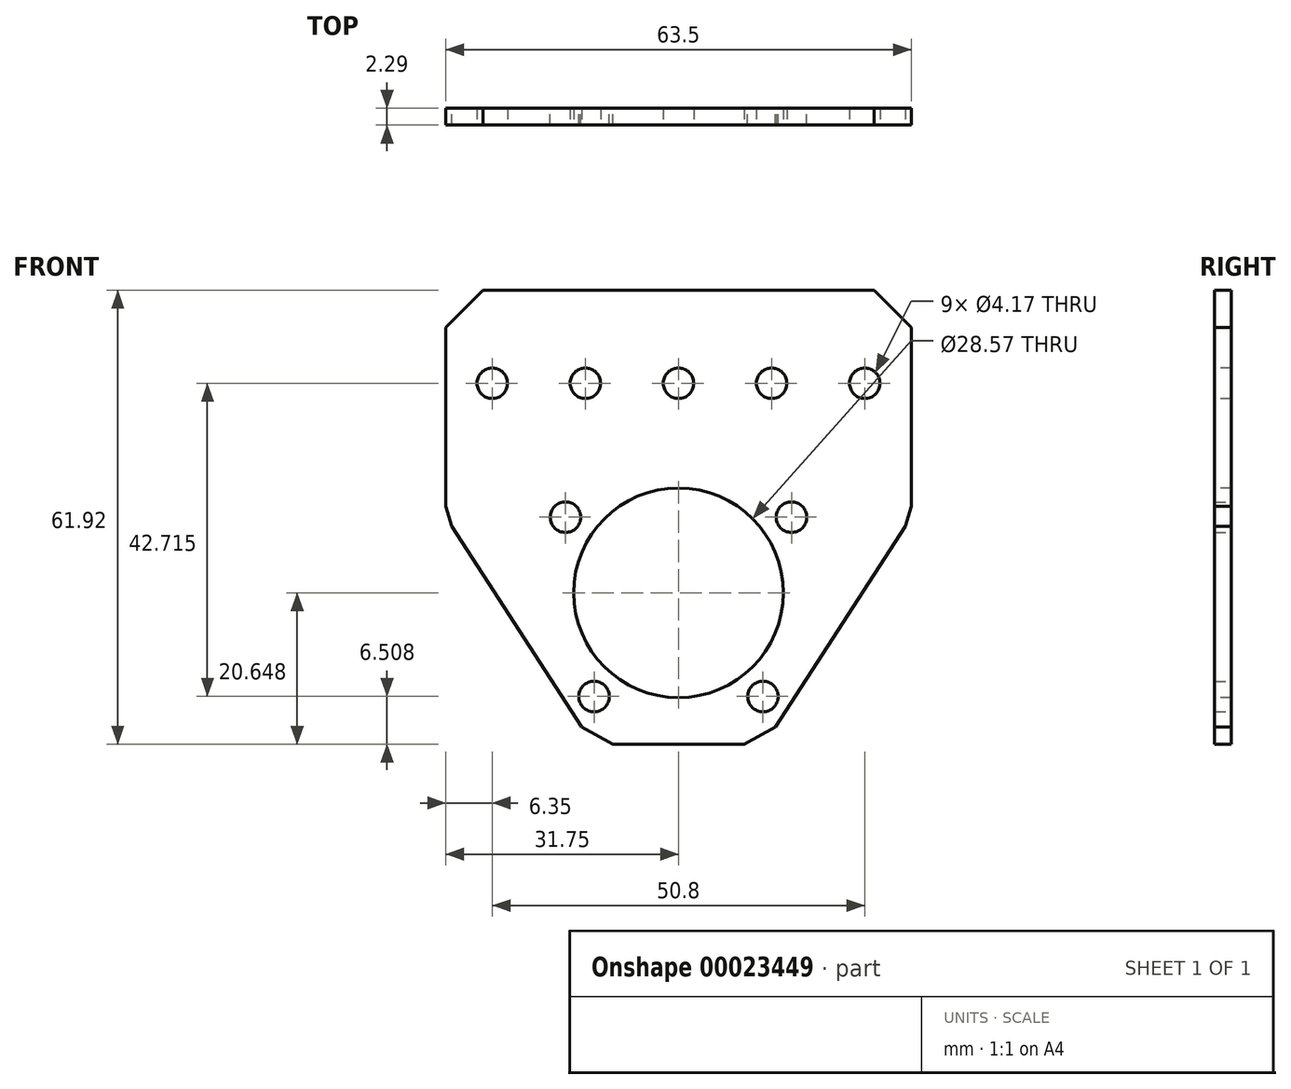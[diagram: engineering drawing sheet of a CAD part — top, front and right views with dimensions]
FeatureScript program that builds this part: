
annotation { "Feature Type Name" : "Feature", "Feature Type Description" : "" }
export const myFeature = defineFeature(function(context is Context, id is Id, definition is map)
    precondition{}
    {
        {
            var Q0;
            Q0=qCreatedBy(makeId("Front.planeOp"),FACE);
            var sketch = newSketch(context, id + "F0", { "sketchPlane" : qUnion([Q0])});
            skLineSegment(sketch, "E0", {"start": v(-31.75, 30.96) * mm, "end": v(31.75, 30.96) * mm});
            skLineSegment(sketch, "E1", {"start": v(31.75, 30.96) * mm, "end": v(31.75, 0) * mm});
            skLineSegment(sketch, "E2", {"start": v(31.75, 0) * mm, "end": v(11.7, -30.96) * mm});
            skLineSegment(sketch, "E3", {"start": v(11.7, -30.96) * mm, "end": v(-11.7, -30.96) * mm});
            skLineSegment(sketch, "E4", {"start": v(-11.7, -30.96) * mm, "end": v(-31.75, 0) * mm});
            skLineSegment(sketch, "E5", {"start": v(-31.75, 0) * mm, "end": v(-31.75, 30.96) * mm});
            skLineSegment(sketch, "E6", {"start": v(0, 34.06) * mm, "end": v(0, -68.88) * mm, "construction": true});
            skLineSegment(sketch, "E7", {"start": v(-50.48, 0) * mm, "end": v(68.05, 0) * mm, "construction": true});
            skSolve(sketch);
        }
        {
            var Q0;
            Q0=makeQuery(id+"F0.imprint","IMPRINT",FACE,{"disambiguationData":[TD([[makeQuery(id+"F0.imprint","IMPRINT",EDGE,{"derivedFrom":sQuery(id+"F0.wireOp",EDGE,"E0")}),-1.0]])]});
            extrude(context, id + "F1", {"entities" : qUnion([Q0]), "depth" : 2.3 * mm});
        }
        {
            var Q0;
            Q0=makeQuery(id+"F1.opExtrude","CAP_FACE",FACE,{"disambiguationData":[OSD([sQuery(id+"F0.wireOp",EDGE,"E0"),sQuery(id+"F0.wireOp",EDGE,"E1"),sQuery(id+"F0.wireOp",EDGE,"E2"),sQuery(id+"F0.wireOp",EDGE,"E3"),sQuery(id+"F0.wireOp",EDGE,"E4"),sQuery(id+"F0.wireOp",EDGE,"E5")])],"isStart":false});
            var sketch = newSketch(context, id + "F2", { "sketchPlane" : qUnion([Q0])});
            skCircle(sketch, "E8", {"center": v(0, -10.31) * mm, "radius": 14.29 * mm});
            skLineSegment(sketch, "E9", {"start": v(-40.4, 18.26) * mm, "end": v(50.03, 18.26) * mm, "construction": true});
            skCircle(sketch, "E10", {"center": v(0, -10.31) * mm, "radius": 18.41 * mm});
            skSolve(sketch);
        }
        {
            var Q0;
            Q0=sQuery(id+"F2.wireOp",VERTEX,"E8.center");
            var Q1;
            Q1=makeQuery(id+"F1.opExtrude","SWEPT_BODY",BODY,{"disambiguationData":[OSD([sQuery(id+"F0.wireOp",EDGE,"E0"),sQuery(id+"F0.wireOp",EDGE,"E1"),sQuery(id+"F0.wireOp",EDGE,"E2"),sQuery(id+"F0.wireOp",EDGE,"E3"),sQuery(id+"F0.wireOp",EDGE,"E4"),sQuery(id+"F0.wireOp",EDGE,"E5")])]});
            hole(context, id + "F3", {"style" : HoleStyle.SIMPLE, "holeDiameter" : 28.57 * mm, "endStyle" : HoleEndStyle.THROUGH, "locations" : qUnion([Q0]), "scope" : qUnion([Q1])});
        }
        {
            var Q0;
            Q0=makeQuery(id+"F1.opExtrude","CAP_FACE",FACE,{"disambiguationData":[OSD([sQuery(id+"F0.wireOp",EDGE,"E0"),sQuery(id+"F0.wireOp",EDGE,"E1"),sQuery(id+"F0.wireOp",EDGE,"E2"),sQuery(id+"F0.wireOp",EDGE,"E3"),sQuery(id+"F0.wireOp",EDGE,"E4"),sQuery(id+"F0.wireOp",EDGE,"E5")])],"isStart":false});
            var sketch = newSketch(context, id + "F4", { "sketchPlane" : qUnion([Q0])});
            skLineSegment(sketch, "E11", {"start": v(-84.78, 18.26) * mm, "end": v(95.41, 18.26) * mm});
            skPoint(sketch, "E12", {"position": v(25.4, 18.26) * mm});
            skPoint(sketch, "E13", {"position": v(12.7, 18.26) * mm});
            skPoint(sketch, "E14", {"position": v(0, 18.26) * mm});
            skPoint(sketch, "E15", {"position": v(-25.4, 18.26) * mm});
            skPoint(sketch, "E16", {"position": v(-12.7, 18.26) * mm});
            skPoint(sketch, "E17", {"position": v(-31.75, 18.26) * mm});
            skPoint(sketch, "E18", {"position": v(31.75, 18.26) * mm});
            skSolve(sketch);
        }
        {
            var Q0;
            Q0=sQuery(id+"F4.wireOp",VERTEX,"E15");
            var Q1;
            Q1=sQuery(id+"F4.wireOp",VERTEX,"E16");
            var Q2;
            Q2=sQuery(id+"F4.wireOp",VERTEX,"E14");
            var Q3;
            Q3=sQuery(id+"F4.wireOp",VERTEX,"E13");
            var Q4;
            Q4=sQuery(id+"F4.wireOp",VERTEX,"E12");
            var Q5;
            Q5=makeQuery(id+"F1.opExtrude","SWEPT_BODY",BODY,{"disambiguationData":[OSD([sQuery(id+"F0.wireOp",EDGE,"E0"),sQuery(id+"F0.wireOp",EDGE,"E1"),sQuery(id+"F0.wireOp",EDGE,"E2"),sQuery(id+"F0.wireOp",EDGE,"E3"),sQuery(id+"F0.wireOp",EDGE,"E4"),sQuery(id+"F0.wireOp",EDGE,"E5")])]});
            hole(context, id + "F5", {"style" : HoleStyle.SIMPLE, "holeDiameter" : 4.17 * mm, "endStyle" : HoleEndStyle.THROUGH, "locations" : qUnion([Q0, Q1, Q2, Q3, Q4]), "scope" : qUnion([Q5])});
        }
        {
            var Q0;
            Q0=qCreatedBy(makeId("Front.planeOp"),FACE);
            var sketch = newSketch(context, id + "F6", { "sketchPlane" : qUnion([Q0])});
            skCircle(sketch, "E19", {"center": v(0, -10.08) * mm, "radius": 18.41 * mm});
            skLineSegment(sketch, "E20", {"start": v(-37.76, 18.5) * mm, "end": v(42.16, 18.5) * mm});
            skPoint(sketch, "E21", {"position": v(31.72, 31.2) * mm});
            skPoint(sketch, "E22", {"position": v(-15.4, 0) * mm});
            skPoint(sketch, "E23", {"position": v(11.52, -24.45) * mm});
            skPoint(sketch, "E24", {"position": v(-11.52, -24.45) * mm});
            skLineSegment(sketch, "E25", {"start": v(0, -40.48) * mm, "end": v(0, 36.9) * mm});
            skLineSegment(sketch, "E26", {"start": v(48.02, -10.08) * mm, "end": v(-38.6, -10.08) * mm});
            skPoint(sketch, "E27", {"position": v(15.4, 0) * mm});
            skSolve(sketch);
        }
        {
            var Q0;
            Q0=sQuery(id+"F6.wireOp",VERTEX,"E22");
            var Q1;
            Q1=sQuery(id+"F6.wireOp",VERTEX,"E27");
            var Q2;
            Q2=sQuery(id+"F6.wireOp",VERTEX,"E23");
            var Q3;
            Q3=sQuery(id+"F6.wireOp",VERTEX,"E24");
            var Q4;
            Q4=makeQuery(id+"F1.opExtrude","SWEPT_BODY",BODY,{"disambiguationData":[OSD([sQuery(id+"F0.wireOp",EDGE,"E0"),sQuery(id+"F0.wireOp",EDGE,"E1"),sQuery(id+"F0.wireOp",EDGE,"E2"),sQuery(id+"F0.wireOp",EDGE,"E3"),sQuery(id+"F0.wireOp",EDGE,"E4"),sQuery(id+"F0.wireOp",EDGE,"E5")])]});
            hole(context, id + "F7", {"style" : HoleStyle.SIMPLE, "holeDiameter" : 4.17 * mm, "endStyle" : HoleEndStyle.THROUGH, "oppositeDirection" : true, "locations" : qUnion([Q0, Q1, Q2, Q3]), "scope" : qUnion([Q4])});
        }
        {
            var Q0;
            Q0=makeQuery(id+"F1.opExtrude","SWEPT_EDGE",EDGE,{"disambiguationData":[OSD([sQuery(id+"F0.wireOp",EDGE,"E0"),sQuery(id+"F0.wireOp",EDGE,"E5")])]});
            var Q1;
            Q1=makeQuery(id+"F1.opExtrude","SWEPT_EDGE",EDGE,{"disambiguationData":[OSD([sQuery(id+"F0.wireOp",EDGE,"E4"),sQuery(id+"F0.wireOp",EDGE,"E5")])]});
            var Q2;
            Q2=makeQuery(id+"F1.opExtrude","SWEPT_EDGE",EDGE,{"disambiguationData":[OSD([sQuery(id+"F0.wireOp",EDGE,"E3"),sQuery(id+"F0.wireOp",EDGE,"E4")])]});
            var Q3;
            Q3=makeQuery(id+"F1.opExtrude","SWEPT_EDGE",EDGE,{"disambiguationData":[OSD([sQuery(id+"F0.wireOp",EDGE,"E2"),sQuery(id+"F0.wireOp",EDGE,"E3")])]});
            var Q4;
            Q4=makeQuery(id+"F1.opExtrude","SWEPT_EDGE",EDGE,{"disambiguationData":[OSD([sQuery(id+"F0.wireOp",EDGE,"E1"),sQuery(id+"F0.wireOp",EDGE,"E2")])]});
            var Q5;
            Q5=makeQuery(id+"F1.opExtrude","SWEPT_EDGE",EDGE,{"disambiguationData":[OSD([sQuery(id+"F0.wireOp",EDGE,"E0"),sQuery(id+"F0.wireOp",EDGE,"E1")])]});
            chamfer(context, id + "F8", {"entities" : qUnion([Q0, Q1, Q2, Q3, Q4, Q5]), "width" : 5.08 * mm, "tangentPropagation" : true});
        }
    });
